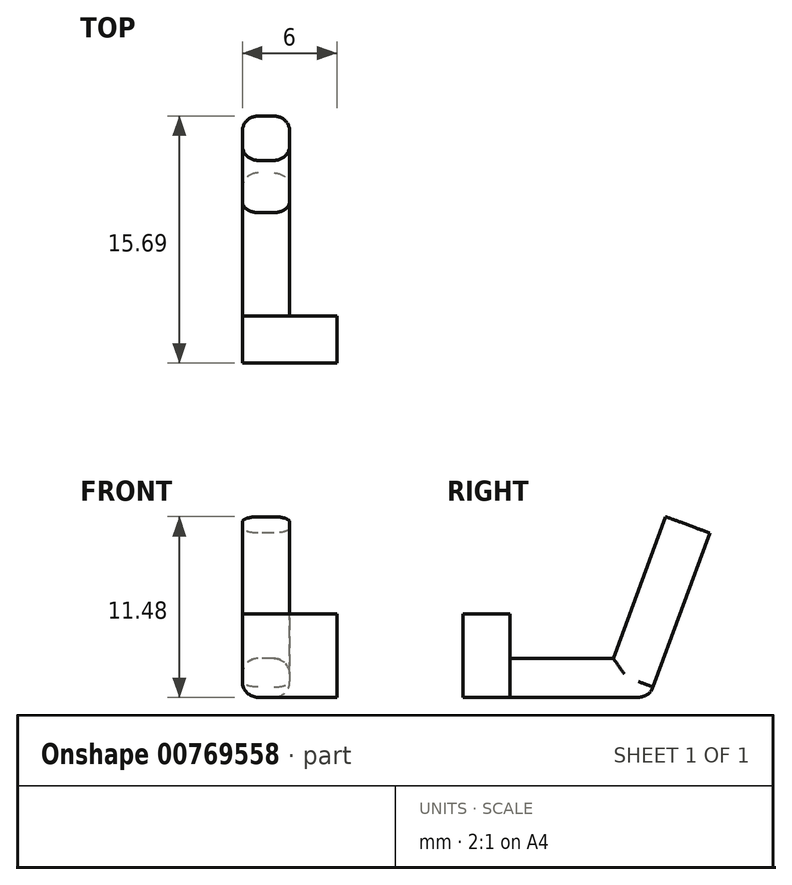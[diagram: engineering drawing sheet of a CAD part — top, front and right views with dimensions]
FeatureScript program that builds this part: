
annotation { "Feature Type Name" : "Feature", "Feature Type Description" : "" }
export const myFeature = defineFeature(function(context is Context, id is Id, definition is map)
    precondition{}
    {
        {
            var Q0;
            Q0=qCreatedBy(makeId("Right.planeOp"),FACE);
            var sketch = newSketch(context, id + "F0", { "sketchPlane" : qUnion([Q0])});
            skLineSegment(sketch, "E0", {"start": v(-15.62, 7.55) * mm, "end": v(-9.06, 7.55) * mm});
            skLineSegment(sketch, "E1", {"start": v(-9.06, 7.55) * mm, "end": v(-5.74, 16.55) * mm});
            skLineSegment(sketch, "E2", {"start": v(-5.74, 16.55) * mm, "end": v(-2.93, 15.5) * mm});
            skLineSegment(sketch, "E3", {"start": v(-2.93, 15.5) * mm, "end": v(-6.77, 5.07) * mm});
            skLineSegment(sketch, "E4", {"start": v(-6.77, 5.07) * mm, "end": v(-18.62, 5.07) * mm});
            skLineSegment(sketch, "E5", {"start": v(-18.62, 5.07) * mm, "end": v(-18.62, 10.39) * mm});
            skLineSegment(sketch, "E6", {"start": v(-18.62, 10.39) * mm, "end": v(-15.62, 10.39) * mm});
            skLineSegment(sketch, "E7", {"start": v(-15.62, 10.39) * mm, "end": v(-15.62, 7.55) * mm});
            skLineSegment(sketch, "E8", {"start": v(-15.62, 7.55) * mm, "end": v(-15.62, 5.07) * mm});
            skLineSegment(sketch, "E9", {"start": v(-15.62, 5.07) * mm, "end": v(-15.62, 7.55) * mm});
            skSolve(sketch);
        }
        {
            var Q0;
            {var subQ0=sQuery(id+"F0.wireOp",EDGE,"E5");Q0=makeQuery(id+"F0.imprint","IMPRINT",FACE,{"disambiguationData":[TD([[makeQuery(id+"F0.imprint","IMPRINT",EDGE,{"derivedFrom":subQ0}),-1.0]])]});}
            extrude(context, id + "F1", {"entities" : qUnion([Q0]), "depth" : 6 * mm, "offsetDistance" : 25.4 * mm});
        }
        {
            var Q0;
            Q0 = qSketchRegion(id + "F0", true);
            extrude(context, id + "F2", {"entities" : qUnion([Q0]), "operationType" : NewBodyOperationType.ADD, "depth" : 3 * mm, "offsetDistance" : 25.4 * mm});
        }
        {
            var Q0;
            Q0=makeQuery(id+"F2.opExtrude","CAP_EDGE",EDGE,{"disambiguationData":[OSD([sQuery(id+"F0.wireOp",EDGE,"E3")])],"isStart":false});
            fillet(context, id + "F3", {"entities" : qUnion([Q0]), "radius" : 1 * mm, "tangentPropagation" : true, "allowEdgeOverflow" : false});
        }
        {
            var Q0;
            Q0=makeQuery(id+"F2.opExtrude","CAP_EDGE",EDGE,{"disambiguationData":[OSD([sQuery(id+"F0.wireOp",EDGE,"E1")])],"isStart":false});
            fillet(context, id + "F4", {"entities" : qUnion([Q0]), "radius" : 1 * mm, "tangentPropagation" : true, "allowEdgeOverflow" : false});
        }
        {
            var Q0;
            Q0=makeQuery(id+"F2.opExtrude","CAP_EDGE",EDGE,{"disambiguationData":[OSD([sQuery(id+"F0.wireOp",EDGE,"E1")])],"isStart":true});
            fillet(context, id + "F5", {"entities" : qUnion([Q0]), "radius" : 1 * mm, "tangentPropagation" : true, "allowEdgeOverflow" : false});
        }
        {
            var Q0;
            Q0=makeQuery(id+"F2.opExtrude","CAP_EDGE",EDGE,{"disambiguationData":[OSD([sQuery(id+"F0.wireOp",EDGE,"E3")])],"isStart":true});
            fillet(context, id + "F6", {"entities" : qUnion([Q0]), "radius" : 1 * mm, "tangentPropagation" : true, "allowEdgeOverflow" : false});
        }
        {
            var Q0;
            Q0=makeQuery(id+"F2.opExtrude","CAP_EDGE",EDGE,{"disambiguationData":[OSD([sQuery(id+"F0.wireOp",EDGE,"E0")])],"isStart":false});
            fillet(context, id + "F7", {"entities" : qUnion([Q0]), "radius" : 1 * mm, "tangentPropagation" : true, "allowEdgeOverflow" : false});
        }
        {
            var Q0;
            Q0=makeQuery(id+"F2.opExtrude","CAP_EDGE",EDGE,{"disambiguationData":[OSD([sQuery(id+"F0.wireOp",EDGE,"E0")])],"isStart":true});
            fillet(context, id + "F8", {"entities" : qUnion([Q0]), "radius" : 1 * mm, "tangentPropagation" : true, "allowEdgeOverflow" : false});
        }
        {
            var Q0;
            Q0=makeQuery(id+"F2.opExtrude","CAP_EDGE",EDGE,{"disambiguationData":[OSD([sQuery(id+"F0.wireOp",EDGE,"E4")])],"isStart":false});
            fillet(context, id + "F9", {"entities" : qUnion([Q0]), "radius" : 1 * mm, "tangentPropagation" : true, "allowEdgeOverflow" : false});
        }
    });
